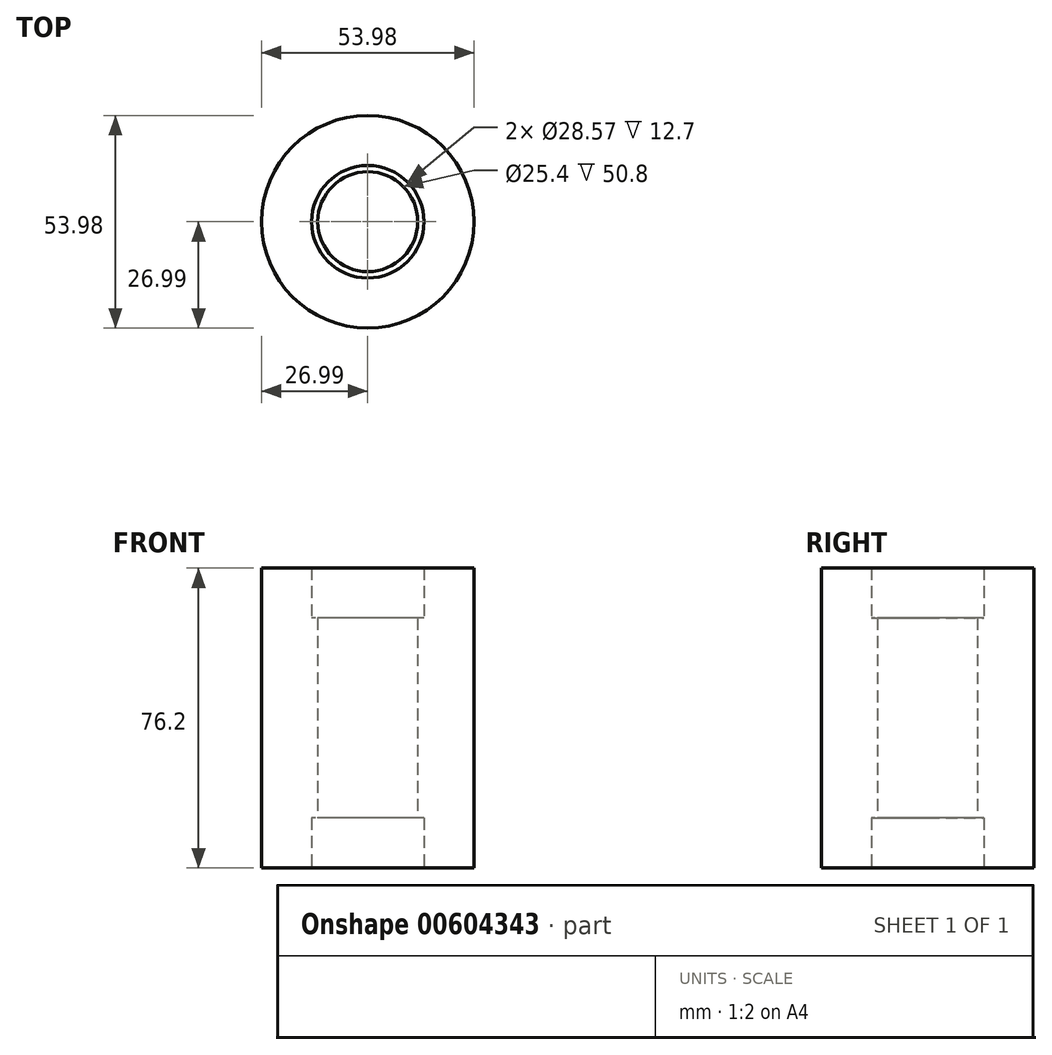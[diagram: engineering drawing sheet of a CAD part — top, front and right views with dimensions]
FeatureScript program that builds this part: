
annotation { "Feature Type Name" : "Feature", "Feature Type Description" : "" }
export const myFeature = defineFeature(function(context is Context, id is Id, definition is map)
    precondition{}
    {
        {
            var Q0;
            Q0=qCreatedBy(makeId("Top.planeOp"),FACE);
            var sketch = newSketch(context, id + "F0", { "sketchPlane" : qUnion([Q0])});
            skLineSegment(sketch, "E0", {"start": v(0, 0) * mm, "end": v(12.7, 0) * mm});
            skCircle(sketch, "E1", {"center": v(0, 0) * mm, "radius": 12.7 * mm});
            skCircle(sketch, "E2.0", {"center": v(0, 0) * mm, "radius": 14.29 * mm});
            skSolve(sketch);
        }
        {
            var Q0;
            Q0=qCreatedBy(makeId("Top.planeOp"),FACE);
            var sketch = newSketch(context, id + "F1", { "sketchPlane" : qUnion([Q0])});
            skSolve(sketch);
        }
        {
            var Q0;
            Q0=qSketchRegion(id+"F1",true);
            var Q1;
            Q1=makeQuery(id+"F0.imprint","IMPRINT",FACE,{"disambiguationData":[TD([[makeQuery(id+"F0.imprint","IMPRINT",EDGE,{"derivedFrom":sQuery(id+"F0.wireOp",EDGE,"E1")}),-1.0]])]});
            extrude(context, id + "F2", {"entities" : qUnion([Q0, Q1]), "depth" : 50.8 * mm, "offsetDistance" : 25.4 * mm});
        }
        {
            var Q0;
            Q0 = qSketchRegion(id + "F0", true);
            var sketch = newSketch(context, id + "F3", { "sketchPlane" : qUnion([Q0])});
            skCircle(sketch, "E3.0", {"center": v(0, 0) * mm, "radius": 26.99 * mm});
            skSolve(sketch);
        }
        {
            var Q0;
            Q0=makeQuery(id+"F3.imprint","IMPRINT",FACE,{"disambiguationData":[TD([[makeQuery(id+"F3.imprint","IMPRINT",EDGE,{"derivedFrom":sQuery(id+"F3.wireOp",EDGE,"E3.0")}),1.0]])]});
            var Q1;
            Q1=sQuery(id+"F0.wireOp",EDGE,"E2.0");
            var Q2;
            Q2=sQuery(id+"F3.wireOp",EDGE,"E3.0");
            extrude(context, id + "F4", {"entities" : qUnion([Q0]), "operationType" : NewBodyOperationType.ADD, "surfaceEntities" : qUnion([Q1, Q2]), "depth" : 63.5 * mm, "offsetDistance" : 25.4 * mm, "hasSecondDirection" : true, "secondDirectionOppositeDirection" : true, "secondDirectionDepth" : 12.7 * mm});
        }
    });
